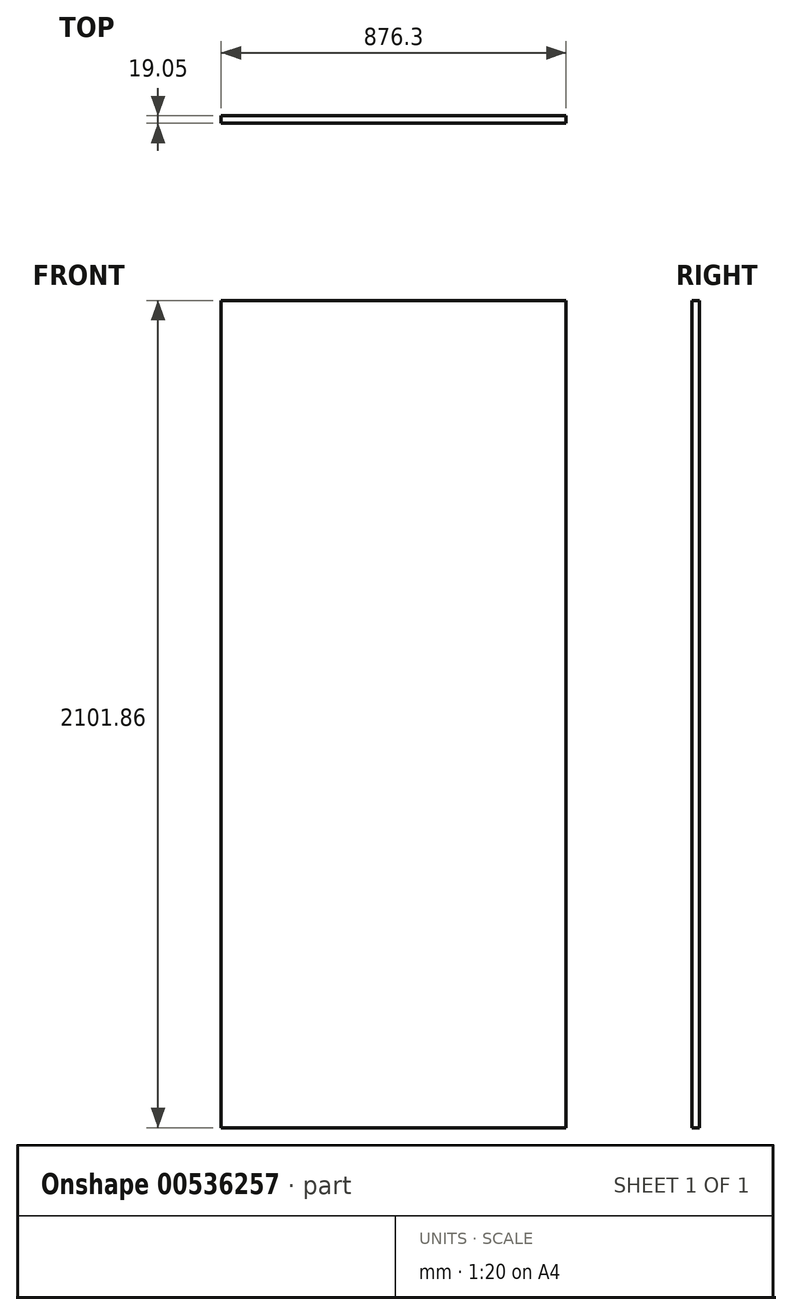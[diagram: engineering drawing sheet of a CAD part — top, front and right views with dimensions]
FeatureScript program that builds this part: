
annotation { "Feature Type Name" : "Feature", "Feature Type Description" : "" }
export const myFeature = defineFeature(function(context is Context, id is Id, definition is map)
    precondition{}
    {
        {
            var Q0;
            Q0=qCreatedBy(makeId("Front.planeOp"),FACE);
            var sketch = newSketch(context, id + "F0", { "sketchPlane" : qUnion([Q0])});
            skLineSegment(sketch, "E0.bottom", {"start": v(428.63, 1050.93) * mm, "end": v(-428.62, 1050.93) * mm});
            skLineSegment(sketch, "E0.top", {"start": v(428.63, -1050.92) * mm, "end": v(-428.62, -1050.92) * mm});
            skLineSegment(sketch, "E0.left", {"start": v(428.63, 1050.93) * mm, "end": v(428.63, -1050.92) * mm});
            skLineSegment(sketch, "E0.right", {"start": v(-428.62, 1050.93) * mm, "end": v(-428.62, -1050.92) * mm});
            skPoint(sketch, "E0.middle", {"position": v(0, 0) * mm});
            skSolve(sketch);
        }
        {
            var Q0;
            Q0 = qSketchRegion(id + "F0", true);
            extrude(context, id + "F1", {"entities" : qUnion([Q0]), "depth" : 19.05 * mm, "offsetDistance" : 25.4 * mm});
        }
        {
            var Q0;
            Q0=makeQuery(id+"F1.opExtrude","SWEPT_FACE",FACE,{"disambiguationData":[OSD([sQuery(id+"F0.wireOp",EDGE,"E0.left")])]});
            extrude(context, id + "F2", {"entities" : qUnion([Q0]), "operationType" : NewBodyOperationType.ADD, "depth" : 19.05 * mm, "offsetDistance" : 25.4 * mm});
        }
    });
